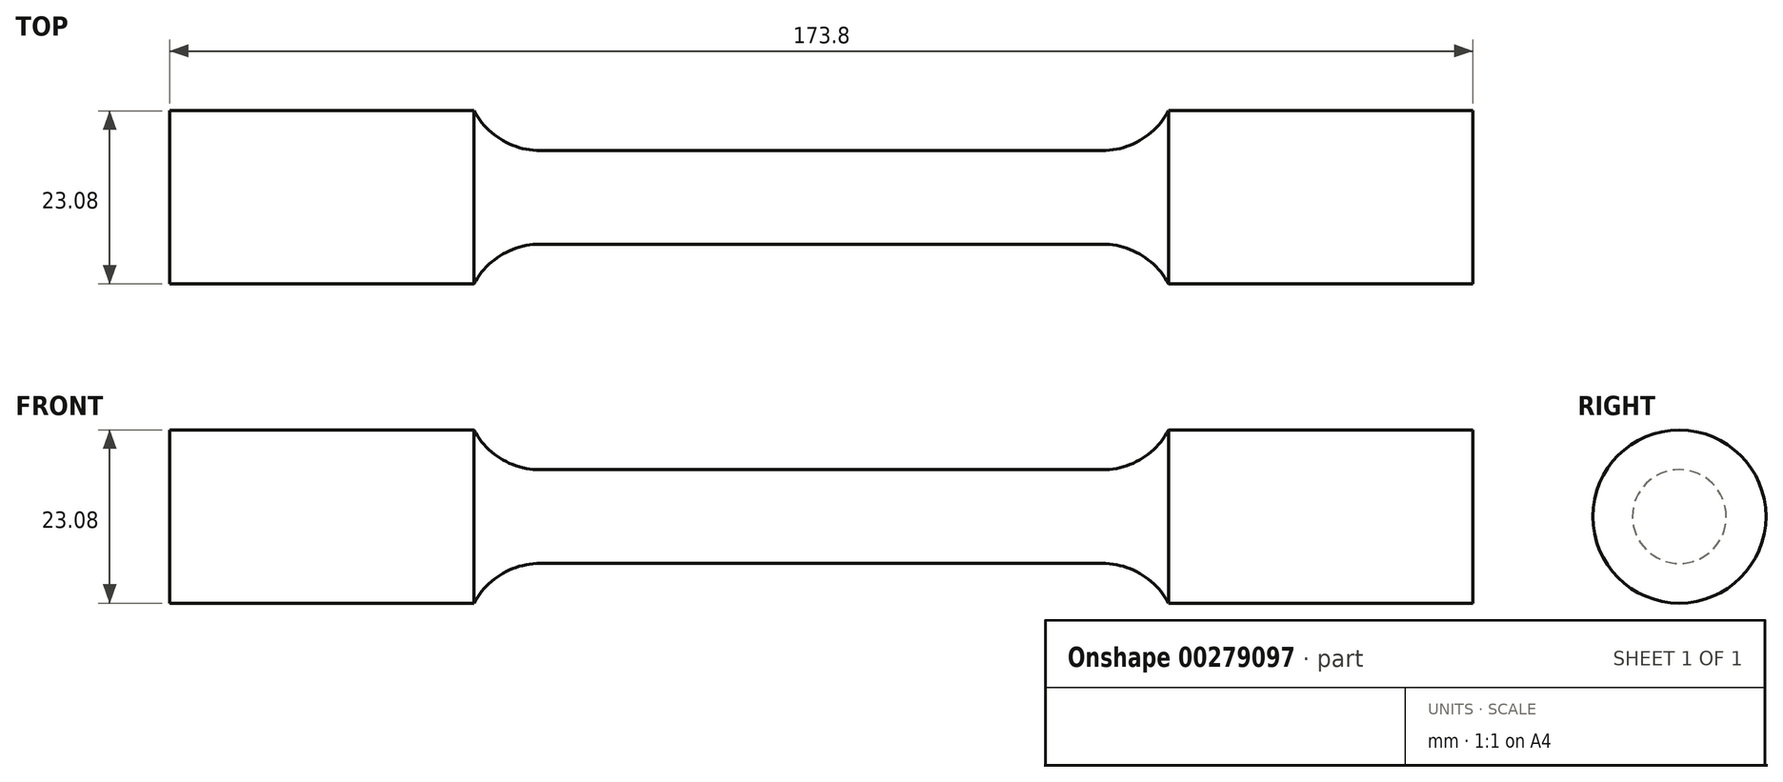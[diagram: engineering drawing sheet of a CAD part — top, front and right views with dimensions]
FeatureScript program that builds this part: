
annotation { "Feature Type Name" : "Feature", "Feature Type Description" : "" }
export const myFeature = defineFeature(function(context is Context, id is Id, definition is map)
    precondition{}
    {
        {
            var Q0;
            Q0=qCreatedBy(makeId("Front.planeOp"),FACE);
            var sketch = newSketch(context, id + "F0", { "sketchPlane" : qUnion([Q0])});
            skLineSegment(sketch, "E0", {"start": v(0, 6.25) * mm, "end": v(37.5, 6.25) * mm});
            skArc(sketch, "E1", {"start": v(37.5, 6.25) * mm, "mid": v(42.64, 7.68) * mm, "end": v(46.32, 11.54) * mm});
            skLineSegment(sketch, "E2", {"start": v(46.32, 11.54) * mm, "end": v(86.9, 11.54) * mm});
            skLineSegment(sketch, "E3", {"start": v(86.9, 11.54) * mm, "end": v(86.9, 0) * mm});
            skLineSegment(sketch, "E4.MirrorCS", {"start": v(-86.9, 11.54) * mm, "end": v(-86.9, 0) * mm});
            skLineSegment(sketch, "E5.MirrorCS", {"start": v(0, 6.25) * mm, "end": v(-37.5, 6.25) * mm});
            skLineSegment(sketch, "E6.MirrorCS", {"start": v(-46.32, 11.54) * mm, "end": v(-86.9, 11.54) * mm});
            skArc(sketch, "E7.MirrorCS", {"start": v(-37.5, 6.25) * mm, "mid": v(-42.64, 7.68) * mm, "end": v(-46.32, 11.54) * mm});
            skLineSegment(sketch, "E8", {"start": v(-86.9, 0) * mm, "end": v(86.9, 0) * mm});
            skSolve(sketch);
        }
        {
            var Q0;
            Q0=makeQuery(id+"F0.imprint","IMPRINT",FACE,{"disambiguationData":[TD([[makeQuery(id+"F0.imprint","IMPRINT",EDGE,{"derivedFrom":sQuery(id+"F0.wireOp",EDGE,"E0")}),-1.0]])]});
            var Q1;
            Q1=sQuery(id+"F0.wireOp",EDGE,"E8");
            revolve(context, id + "F1", {"entities" : qUnion([Q0]), "axis" : qUnion([Q1]), "revolveType" : RevolveType.FULL});
        }
    });
